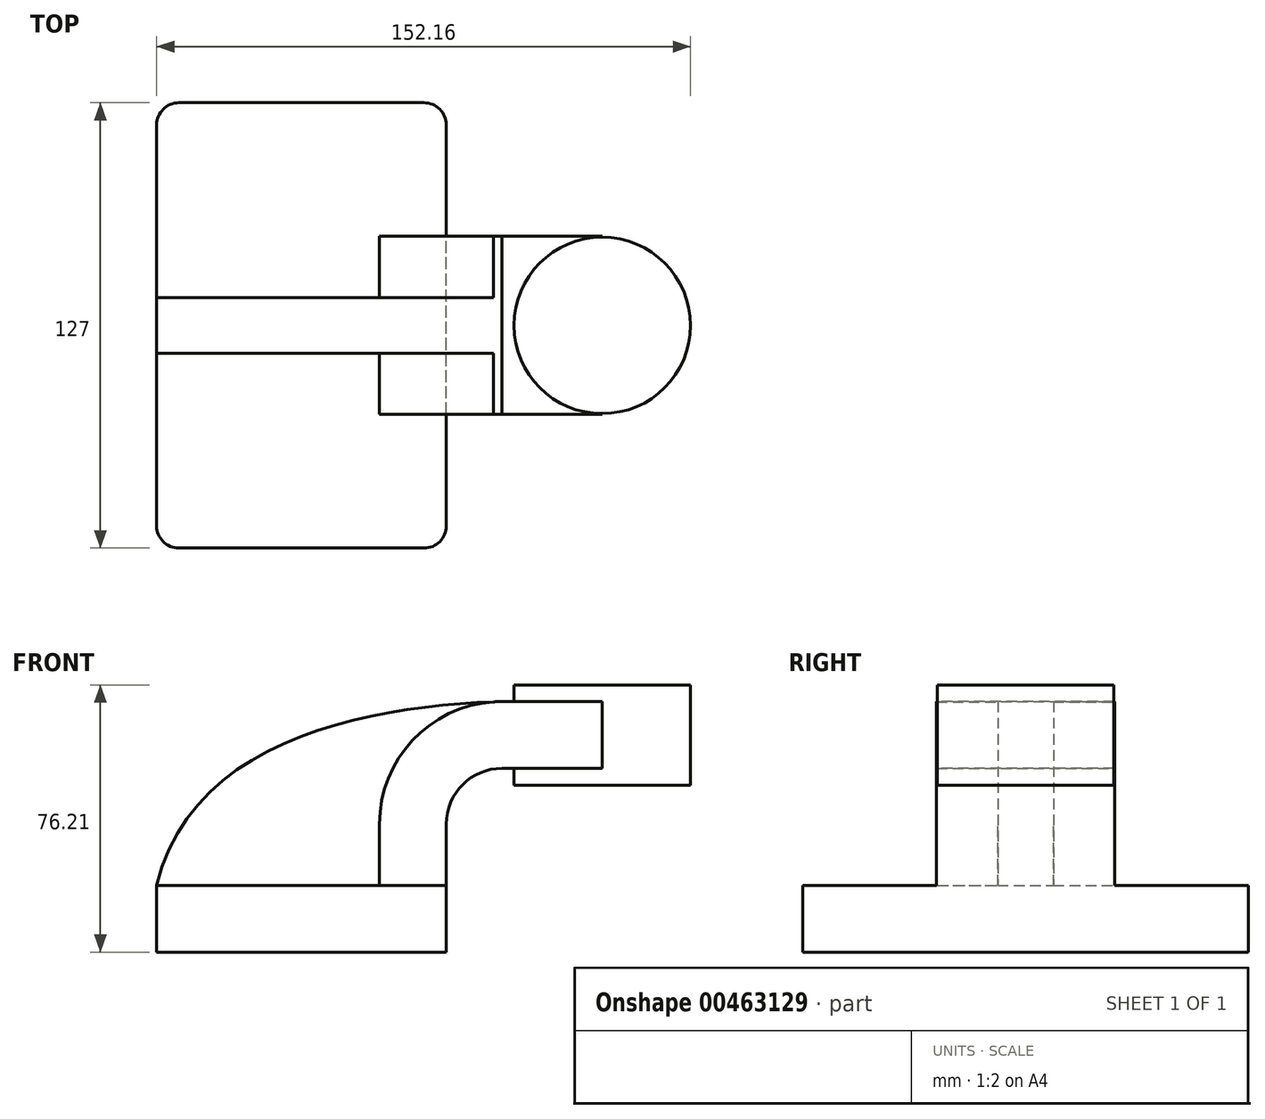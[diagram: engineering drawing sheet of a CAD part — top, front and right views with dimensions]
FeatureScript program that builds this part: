
annotation { "Feature Type Name" : "Feature", "Feature Type Description" : "" }
export const myFeature = defineFeature(function(context is Context, id is Id, definition is map)
    precondition{}
    {
        {
            var Q0;
            Q0=qCreatedBy(makeId("Front.planeOp"),FACE);
            var sketch = newSketch(context, id + "F0", { "sketchPlane" : qUnion([Q0])});
            skLineSegment(sketch, "E0.bottom", {"start": v(41.27, 9.53) * mm, "end": v(-41.28, 9.53) * mm});
            skLineSegment(sketch, "E0.top", {"start": v(41.28, -9.52) * mm, "end": v(-41.27, -9.52) * mm});
            skLineSegment(sketch, "E0.left", {"start": v(41.27, 9.53) * mm, "end": v(41.28, -9.52) * mm});
            skLineSegment(sketch, "E0.right", {"start": v(-41.28, 9.53) * mm, "end": v(-41.27, -9.52) * mm});
            skPoint(sketch, "E0.middle", {"position": v(0, 0) * mm});
            skLineSegment(sketch, "E1.bottom", {"start": v(110.88, 38.1) * mm, "end": v(60.08, 38.1) * mm});
            skLineSegment(sketch, "E1.top", {"start": v(110.88, 66.68) * mm, "end": v(60.08, 66.68) * mm});
            skLineSegment(sketch, "E1.left", {"start": v(110.88, 38.1) * mm, "end": v(110.88, 66.67) * mm});
            skLineSegment(sketch, "E1.right", {"start": v(60.08, 38.1) * mm, "end": v(60.08, 66.67) * mm});
            skPoint(sketch, "E1.middle", {"position": v(85.48, 52.39) * mm});
            skLineSegment(sketch, "E2", {"start": v(41.27, 9.53) * mm, "end": v(41.27, 27) * mm});
            skArc(sketch, "E3", {"start": v(41.27, 27) * mm, "mid": v(45.92, 38.23) * mm, "end": v(57.15, 42.88) * mm});
            skLineSegment(sketch, "E4", {"start": v(57.15, 42.88) * mm, "end": v(85.73, 42.88) * mm});
            skLineSegment(sketch, "E5.0", {"start": v(57.15, 61.93) * mm, "end": v(85.73, 61.93) * mm});
            skArc(sketch, "E5.1", {"start": v(22.22, 27) * mm, "mid": v(32.45, 51.7) * mm, "end": v(57.15, 61.93) * mm});
            skLineSegment(sketch, "E5.2", {"start": v(22.22, 9.53) * mm, "end": v(22.22, 27) * mm});
            skLineSegment(sketch, "E6", {"start": v(85.73, 66.68) * mm, "end": v(85.73, 38.1) * mm});
            skFitSpline(sketch, "E7", {"points": [v(57.15, 61.93) * mm, v(-41.28, 9.53) * mm], "startDerivative": vector(-106.15, -3.2) * mm, "endDerivative": vector(-30.94, -128.94) * mm});
            skSolve(sketch);
        }
        {
            var Q0;
            Q0=makeQuery(id+"F0.imprint","IMPRINT",FACE,{"disambiguationData":[TD([[makeQuery(id+"F0.imprint","IMPRINT",EDGE,{"derivedFrom":sQuery(id+"F0.wireOp",EDGE,"E0.top")}),-1.0]])]});
            extrude(context, id + "F1", {"entities" : qUnion([Q0]), "endBound" : BoundingType.SYMMETRIC, "depth" : 127 * mm});
        }
        {
            var Q0;
            {var subQ6=sQuery(id+"F0.wireOp",EDGE,"E2");Q0=makeQuery(id+"F0.imprint","IMPRINT",FACE,{"disambiguationData":[TD([[makeQuery(id+"F0.imprint","IMPRINT",EDGE,{"derivedFrom":subQ6}),1.0]])]});}
            extrude(context, id + "F2", {"entities" : qUnion([Q0]), "operationType" : NewBodyOperationType.ADD, "endBound" : BoundingType.SYMMETRIC, "depth" : 50.8 * mm});
        }
        {
            var Q0;
            {var subQ3=sQuery(id+"F0.wireOp",EDGE,"E5.2");Q0=makeQuery(id+"F0.imprint","IMPRINT",FACE,{"disambiguationData":[TD([[makeQuery(id+"F0.imprint","IMPRINT",EDGE,{"derivedFrom":subQ3}),1.0]])]});}
            extrude(context, id + "F3", {"entities" : qUnion([Q0]), "operationType" : NewBodyOperationType.ADD, "endBound" : BoundingType.SYMMETRIC, "depth" : 15.88 * mm});
        }
        {
            var Q0;
            {var subQ0=sQuery(id+"F0.wireOp",EDGE,"E4");var subQ1=sQuery(id+"F0.wireOp",EDGE,"E1.right");var subQ2=makeQuery(id+"F0.imprint","INTERSECT",VERTEX,{"derivedFrom":[subQ1,subQ0]});Q0=makeQuery(id+"F0.imprint","IMPRINT",FACE,{"disambiguationData":[TD([[makeQuery(id+"F0.imprint","IMPRINT",EDGE,{"disambiguationData":[TD([[subQ2,-1.0]])],"derivedFrom":subQ1}),-1.0]])]});}
            extrude(context, id + "F4", {"entities" : qUnion([Q0]), "operationType" : NewBodyOperationType.ADD, "endBound" : BoundingType.SYMMETRIC, "depth" : 50.8 * mm});
        }
        {
            var Q0;
            {var subQ0=sQuery(id+"F0.wireOp",EDGE,"E1.left");Q0=makeQuery(id+"F0.imprint","IMPRINT",FACE,{"disambiguationData":[TD([[makeQuery(id+"F0.imprint","IMPRINT",EDGE,{"derivedFrom":subQ0}),1.0]])]});}
            var Q1;
            Q1=sQuery(id+"F0.wireOp",EDGE,"E6");
            revolve(context, id + "F5", {"operationType" : NewBodyOperationType.ADD, "entities" : qUnion([Q0]), "axis" : qUnion([Q1]), "revolveType" : RevolveType.FULL});
        }
        {
            var Q0;
            Q0=makeQuery(id+"F1.opExtrude","CAP_EDGE",EDGE,{"disambiguationData":[OSD([sQuery(id+"F0.wireOp",EDGE,"E0.left")])],"isStart":false});
            var Q1;
            Q1=makeQuery(id+"F1.opExtrude","CAP_EDGE",EDGE,{"disambiguationData":[OSD([sQuery(id+"F0.wireOp",EDGE,"E0.right")])],"isStart":false});
            var Q2;
            Q2=makeQuery(id+"F1.opExtrude","CAP_EDGE",EDGE,{"disambiguationData":[OSD([sQuery(id+"F0.wireOp",EDGE,"E0.left")])],"isStart":true});
            var Q3;
            Q3=makeQuery(id+"F1.opExtrude","CAP_EDGE",EDGE,{"disambiguationData":[OSD([sQuery(id+"F0.wireOp",EDGE,"E0.right")])],"isStart":true});
            fillet(context, id + "F6", {"entities" : qUnion([Q0, Q1, Q2, Q3]), "radius" : 6.35 * mm, "tangentPropagation" : true, "allowEdgeOverflow" : false});
        }
    });
